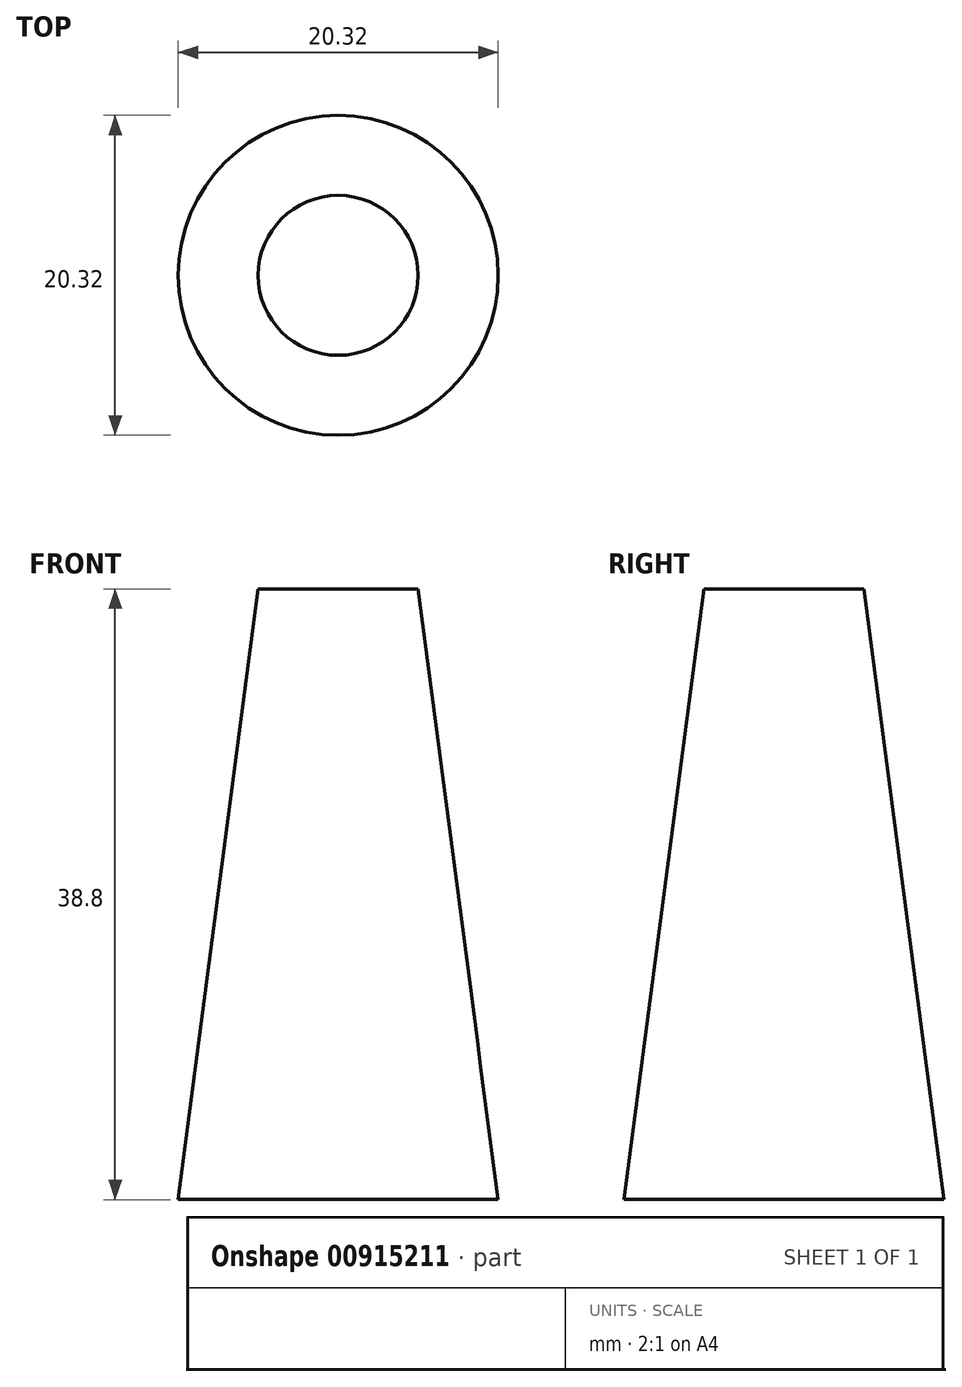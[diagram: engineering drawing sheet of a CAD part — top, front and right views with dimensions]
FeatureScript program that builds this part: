
annotation { "Feature Type Name" : "Feature", "Feature Type Description" : "" }
export const myFeature = defineFeature(function(context is Context, id is Id, definition is map)
    precondition{}
    {
        {
            var Q0;
            Q0=qCreatedBy(makeId("Front.planeOp"),FACE);
            var sketch = newSketch(context, id + "F0", { "sketchPlane" : qUnion([Q0])});
            skLineSegment(sketch, "E0", {"start": v(0, 42.67) * mm, "end": v(0, -39.68) * mm, "construction": true});
            skLineSegment(sketch, "E1", {"start": v(-39.88, 0) * mm, "end": v(46.41, 0) * mm, "construction": true});
            skLineSegment(sketch, "E2", {"start": v(0, 20.29) * mm, "end": v(-5.08, 20.29) * mm});
            skLineSegment(sketch, "E3", {"start": v(-5.08, 20.29) * mm, "end": v(-10.16, -18.5) * mm});
            skLineSegment(sketch, "E4", {"start": v(-10.16, -18.5) * mm, "end": v(0, -18.5) * mm});
            skLineSegment(sketch, "E5", {"start": v(0, -18.5) * mm, "end": v(0, 20.29) * mm});
            skSolve(sketch);
        }
        {
            var Q0;
            Q0=makeQuery(id+"F0.imprint","IMPRINT",FACE,{"disambiguationData":[TD([[makeQuery(id+"F0.imprint","IMPRINT",EDGE,{"derivedFrom":sQuery(id+"F0.wireOp",EDGE,"E2")}),1.0]])]});
            var Q1;
            Q1=sQuery(id+"F0.wireOp",EDGE,"E0");
            revolve(context, id + "F1", {"surfaceOperationType" : NewSurfaceOperationType.NEW, "entities" : qUnion([Q0]), "axis" : qUnion([Q1]), "revolveType" : RevolveType.FULL});
        }
    });
